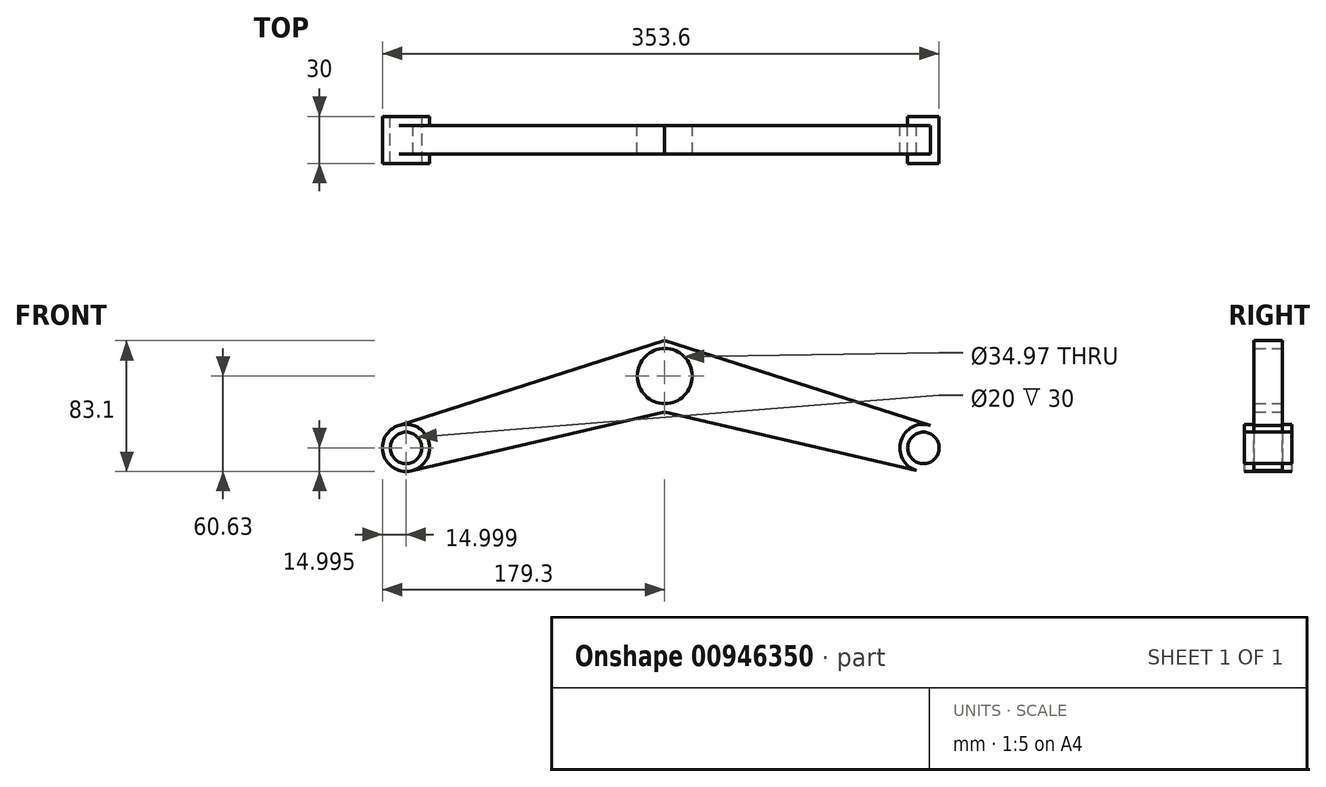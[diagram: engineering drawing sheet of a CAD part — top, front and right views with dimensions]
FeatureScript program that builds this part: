
annotation { "Feature Type Name" : "Feature", "Feature Type Description" : "" }
export const myFeature = defineFeature(function(context is Context, id is Id, definition is map)
    precondition{}
    {
        {
            var Q0;
            Q0=qCreatedBy(makeId("Front.planeOp"),FACE);
            var sketch = newSketch(context, id + "F0", { "sketchPlane" : qUnion([Q0])});
            skLineSegment(sketch, "E0", {"start": v(0, 0) * mm, "end": v(-159.75, -37.02) * mm});
            skLineSegment(sketch, "E1", {"start": v(0, 45.38) * mm, "end": v(-168.86, -8.43) * mm});
            skCircle(sketch, "E2", {"center": v(0, 22.9) * mm, "radius": 10 * mm});
            skCircle(sketch, "E3", {"center": v(0, 22.9) * mm, "radius": 17.49 * mm});
            skLineSegment(sketch, "E4", {"start": v(0, 60.15) * mm, "end": v(0, -65.38) * mm, "construction": true});
            skCircle(sketch, "E5", {"center": v(-164.3, -22.72) * mm, "radius": 15 * mm});
            skCircle(sketch, "E6", {"center": v(-164.3, -22.72) * mm, "radius": 10 * mm});
            skLineSegment(sketch, "E7", {"start": v(-168.86, -8.43) * mm, "end": v(-159.75, -37.02) * mm, "construction": true});
            skLineSegment(sketch, "E8.MirrorCS", {"start": v(168.86, -8.43) * mm, "end": v(159.75, -37.02) * mm, "construction": true});
            skLineSegment(sketch, "E9.MirrorCS", {"start": v(0, 0) * mm, "end": v(159.75, -37.02) * mm});
            skLineSegment(sketch, "E10.MirrorCS", {"start": v(0, 45.38) * mm, "end": v(168.86, -8.43) * mm});
            skCircle(sketch, "E11.MirrorC", {"center": v(164.3, -22.72) * mm, "radius": 15 * mm});
            skCircle(sketch, "E12.MirrorC", {"center": v(164.3, -22.72) * mm, "radius": 10 * mm});
            skSolve(sketch);
        }
        {
            var Q0;
            {var subQ1=sQuery(id+"F0.wireOp",EDGE,"E0");Q0=makeQuery(id+"F0.imprint","IMPRINT",FACE,{"disambiguationData":[TD([[makeQuery(id+"F0.imprint","IMPRINT",EDGE,{"derivedFrom":subQ1}),-1.0]])]});}
            extrude(context, id + "F1", {"entities" : qUnion([Q0]), "endBound" : BoundingType.SYMMETRIC, "depth" : 18 * mm, "offsetDistance" : 25 * mm});
        }
        {
            var Q0;
            Q0=makeQuery(id+"F0.imprint","IMPRINT",FACE,{"disambiguationData":[TD([[makeQuery(id+"F0.imprint","IMPRINT",EDGE,{"derivedFrom":sQuery(id+"F0.wireOp",EDGE,"E6")}),-1.0]])]});
            var Q1;
            Q1=makeQuery(id+"F0.imprint","IMPRINT",FACE,{"disambiguationData":[TD([[makeQuery(id+"F0.imprint","IMPRINT",EDGE,{"derivedFrom":sQuery(id+"F0.wireOp",EDGE,"E3")}),-1.0]])]});
            var Q2;
            Q2=makeQuery(id+"F0.imprint","IMPRINT",FACE,{"disambiguationData":[TD([[makeQuery(id+"F0.imprint","IMPRINT",EDGE,{"derivedFrom":sQuery(id+"F0.wireOp",EDGE,"E12.MirrorC")}),1.0]])]});
            extrude(context, id + "F2", {"entities" : qUnion([Q0, Q1, Q2]), "operationType" : NewBodyOperationType.ADD, "endBound" : BoundingType.SYMMETRIC, "depth" : 30 * mm, "offsetDistance" : 25 * mm});
        }
    });
